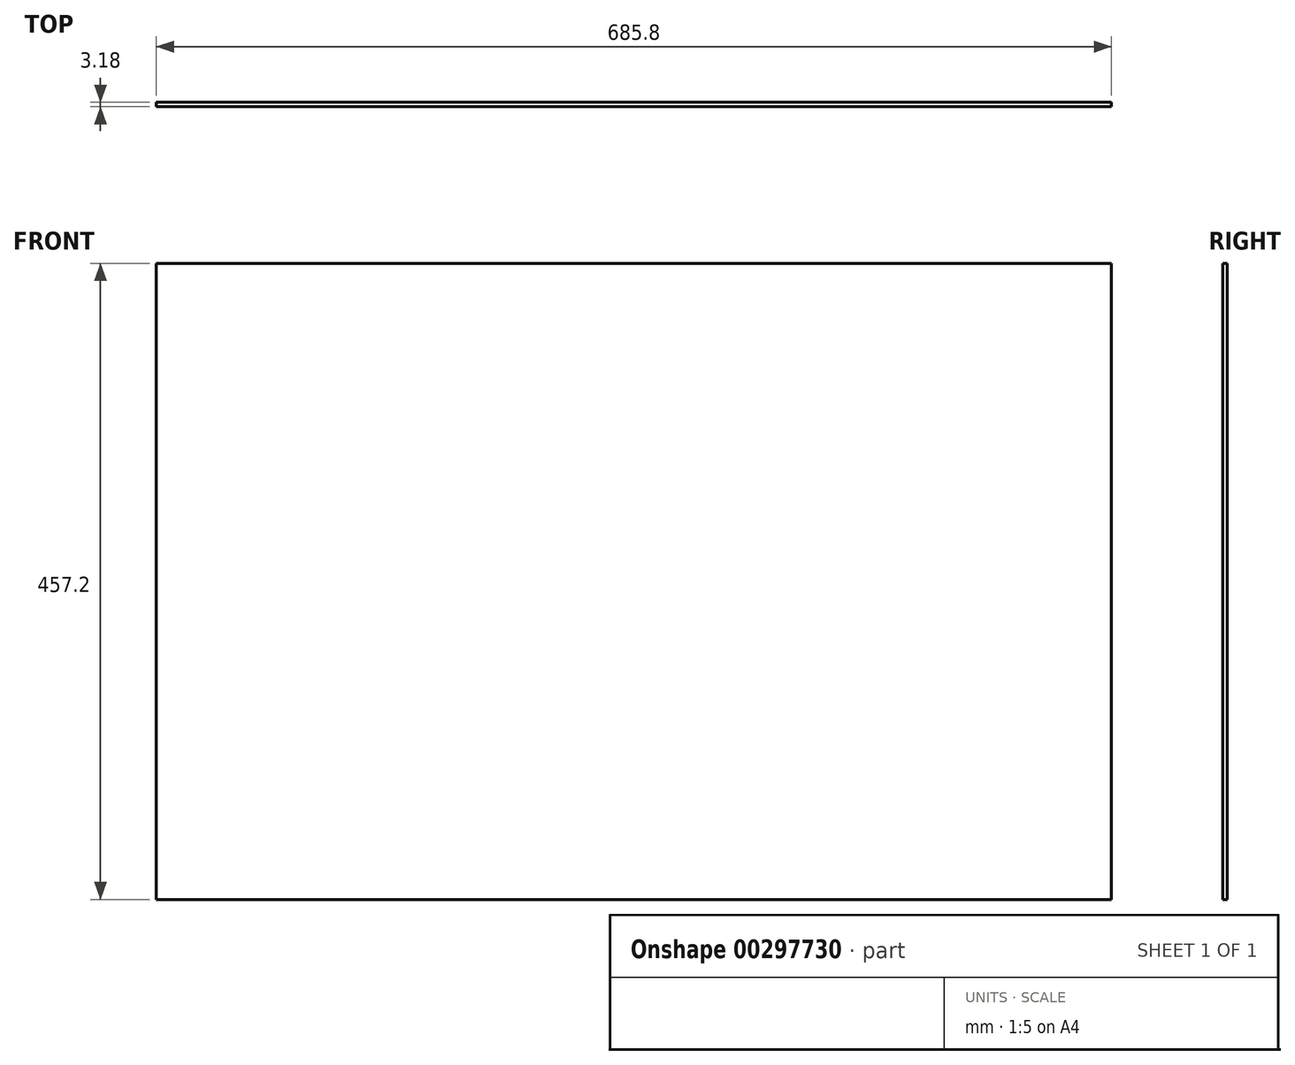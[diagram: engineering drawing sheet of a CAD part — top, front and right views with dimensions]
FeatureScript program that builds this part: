
annotation { "Feature Type Name" : "Feature", "Feature Type Description" : "" }
export const myFeature = defineFeature(function(context is Context, id is Id, definition is map)
    precondition{}
    {
        {
            var Q0;
            Q0=qCreatedBy(makeId("Front.planeOp"),FACE);
            var sketch = newSketch(context, id + "F0", { "sketchPlane" : qUnion([Q0])});
            skLineSegment(sketch, "E0.bottom", {"start": v(342.9, -228.6) * mm, "end": v(-342.9, -228.6) * mm});
            skLineSegment(sketch, "E0.top", {"start": v(342.9, 228.6) * mm, "end": v(-342.9, 228.6) * mm});
            skLineSegment(sketch, "E0.left", {"start": v(342.9, -228.6) * mm, "end": v(342.9, 228.6) * mm});
            skLineSegment(sketch, "E0.right", {"start": v(-342.9, -228.6) * mm, "end": v(-342.9, 228.6) * mm});
            skPoint(sketch, "E0.middle", {"position": v(0, 0) * mm});
            skSolve(sketch);
        }
        {
            var Q0;
            Q0=makeQuery(id+"F0.imprint","IMPRINT",FACE,{"disambiguationData":[TD([[makeQuery(id+"F0.imprint","IMPRINT",EDGE,{"derivedFrom":sQuery(id+"F0.wireOp",EDGE,"E0.bottom")}),-1.0]])]});
            extrude(context, id + "F1", {"entities" : qUnion([Q0]), "endBound" : BoundingType.SYMMETRIC, "depth" : 3.17 * mm});
        }
    });
